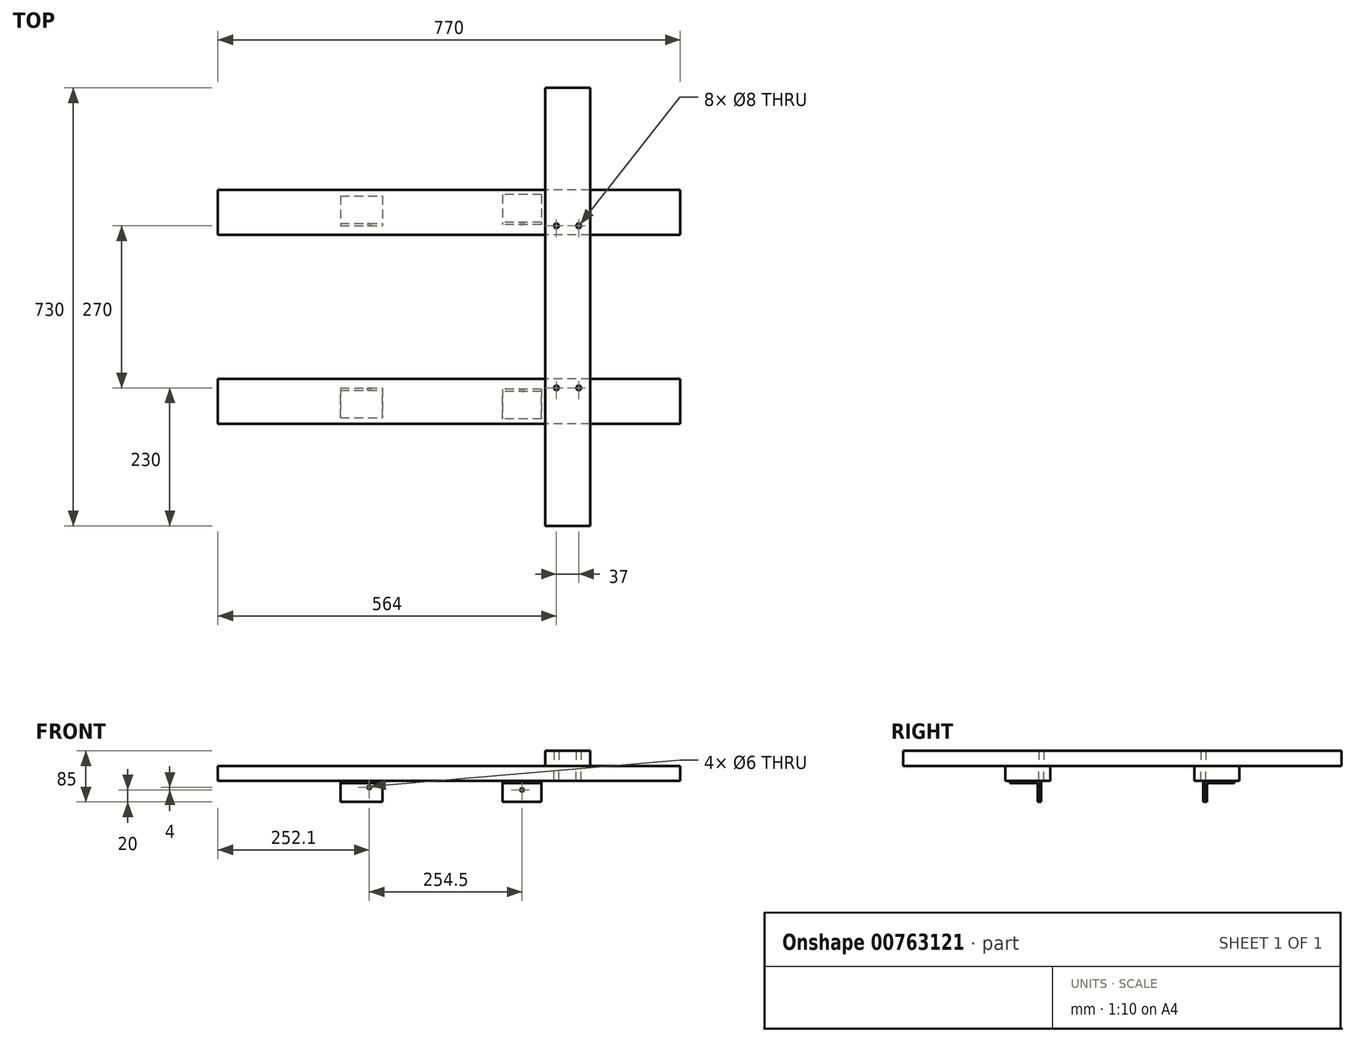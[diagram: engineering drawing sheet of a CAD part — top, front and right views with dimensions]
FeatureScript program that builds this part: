
annotation { "Feature Type Name" : "Feature", "Feature Type Description" : "" }
export const myFeature = defineFeature(function(context is Context, id is Id, definition is map)
    precondition{}
    {
        {
            var Q0;
            Q0=qCreatedBy(makeId("Top.planeOp"),FACE);
            var sketch = newSketch(context, id + "F0", { "sketchPlane" : qUnion([Q0])});
            skLineSegment(sketch, "E0.bottom", {"start": v(145.9, -365) * mm, "end": v(70.9, -365) * mm});
            skLineSegment(sketch, "E0.top", {"start": v(145.9, 365) * mm, "end": v(70.9, 365) * mm});
            skLineSegment(sketch, "E0.left", {"start": v(145.9, -365) * mm, "end": v(145.9, 365) * mm});
            skLineSegment(sketch, "E0.right", {"start": v(70.9, -365) * mm, "end": v(70.9, 365) * mm});
            skPoint(sketch, "E0.middle", {"position": v(108.4, 0) * mm});
            skLineSegment(sketch, "E1.bottom", {"start": v(295.9, 120) * mm, "end": v(-474.1, 120) * mm});
            skLineSegment(sketch, "E1.top", {"start": v(295.9, 195) * mm, "end": v(-474.1, 195) * mm});
            skLineSegment(sketch, "E1.left", {"start": v(295.9, 120) * mm, "end": v(295.9, 195) * mm});
            skLineSegment(sketch, "E1.right", {"start": v(-474.1, 120) * mm, "end": v(-474.1, 195) * mm});
            skPoint(sketch, "E1.middle", {"position": v(-89.1, 157.5) * mm});
            skLineSegment(sketch, "E2.bottom", {"start": v(295.9, -195) * mm, "end": v(-474.1, -195) * mm});
            skLineSegment(sketch, "E2.top", {"start": v(295.9, -120) * mm, "end": v(-474.1, -120) * mm});
            skLineSegment(sketch, "E2.left", {"start": v(295.9, -195) * mm, "end": v(295.9, -120) * mm});
            skLineSegment(sketch, "E2.right", {"start": v(-474.1, -195) * mm, "end": v(-474.1, -120) * mm});
            skPoint(sketch, "E2.middle", {"position": v(-89.1, -157.5) * mm});
            skPoint(sketch, "E3", {"position": v(89.9, 135) * mm});
            skPoint(sketch, "E4", {"position": v(126.9, 135) * mm});
            skPoint(sketch, "E5", {"position": v(89.9, -135) * mm});
            skPoint(sketch, "E6", {"position": v(126.9, -135) * mm});
            skSolve(sketch);
        }
        {
            var Q0;
            {var subQ5=sQuery(id+"F0.wireOp",EDGE,"E1.right");Q0=makeQuery(id+"F0.imprint","IMPRINT",FACE,{"disambiguationData":[TD([[makeQuery(id+"F0.imprint","IMPRINT",EDGE,{"derivedFrom":subQ5}),-1.0]])]});}
            var Q1;
            {var subQ0=sQuery(id+"F0.wireOp",EDGE,"E1.bottom");var subQ1=sQuery(id+"F0.wireOp",EDGE,"E0.left");var subQ2=makeQuery(id+"F0.imprint","INTERSECT",VERTEX,{"derivedFrom":[subQ1,subQ0]});Q1=makeQuery(id+"F0.imprint","IMPRINT",FACE,{"disambiguationData":[TD([[makeQuery(id+"F0.imprint","IMPRINT",EDGE,{"disambiguationData":[TD([[subQ2,-1.0]])],"derivedFrom":subQ1}),1.0]])]});}
            var Q2;
            {var subQ5=sQuery(id+"F0.wireOp",EDGE,"E1.left");Q2=makeQuery(id+"F0.imprint","IMPRINT",FACE,{"disambiguationData":[TD([[makeQuery(id+"F0.imprint","IMPRINT",EDGE,{"derivedFrom":subQ5}),1.0]])]});}
            var Q3;
            {var subQ5=sQuery(id+"F0.wireOp",EDGE,"E2.right");Q3=makeQuery(id+"F0.imprint","IMPRINT",FACE,{"disambiguationData":[TD([[makeQuery(id+"F0.imprint","IMPRINT",EDGE,{"derivedFrom":subQ5}),-1.0]])]});}
            var Q4;
            {var subQ0=sQuery(id+"F0.wireOp",EDGE,"E2.bottom");var subQ1=sQuery(id+"F0.wireOp",EDGE,"E0.left");var subQ2=makeQuery(id+"F0.imprint","INTERSECT",VERTEX,{"derivedFrom":[subQ1,subQ0]});Q4=makeQuery(id+"F0.imprint","IMPRINT",FACE,{"disambiguationData":[TD([[makeQuery(id+"F0.imprint","IMPRINT",EDGE,{"disambiguationData":[TD([[subQ2,-1.0]])],"derivedFrom":subQ1}),1.0]])]});}
            var Q5;
            {var subQ5=sQuery(id+"F0.wireOp",EDGE,"E2.left");Q5=makeQuery(id+"F0.imprint","IMPRINT",FACE,{"disambiguationData":[TD([[makeQuery(id+"F0.imprint","IMPRINT",EDGE,{"derivedFrom":subQ5}),1.0]])]});}
            extrude(context, id + "F1", {"entities" : qUnion([Q0, Q1, Q2, Q3, Q4, Q5]), "oppositeDirection" : true, "depth" : 25 * mm, "offsetDistance" : 25 * mm});
        }
        {
            var Q0;
            {var subQ0=sQuery(id+"F0.wireOp",EDGE,"E1.bottom");var subQ1=sQuery(id+"F0.wireOp",EDGE,"E0.left");var subQ2=makeQuery(id+"F0.imprint","INTERSECT",VERTEX,{"derivedFrom":[subQ1,subQ0]});Q0=makeQuery(id+"F0.imprint","IMPRINT",FACE,{"disambiguationData":[TD([[makeQuery(id+"F0.imprint","IMPRINT",EDGE,{"disambiguationData":[TD([[subQ2,-1.0]])],"derivedFrom":subQ1}),1.0]])]});}
            var Q1;
            {var subQ0=sQuery(id+"F0.wireOp",EDGE,"E0.top");Q1=makeQuery(id+"F0.imprint","IMPRINT",FACE,{"disambiguationData":[TD([[makeQuery(id+"F0.imprint","IMPRINT",EDGE,{"derivedFrom":subQ0}),1.0]])]});}
            var Q2;
            {var subQ0=sQuery(id+"F0.wireOp",EDGE,"E2.top");var subQ1=sQuery(id+"F0.wireOp",EDGE,"E0.left");var subQ2=makeQuery(id+"F0.imprint","INTERSECT",VERTEX,{"derivedFrom":[subQ1,subQ0]});Q2=makeQuery(id+"F0.imprint","IMPRINT",FACE,{"disambiguationData":[TD([[makeQuery(id+"F0.imprint","IMPRINT",EDGE,{"disambiguationData":[TD([[subQ2,-1.0]])],"derivedFrom":subQ1}),1.0]])]});}
            var Q3;
            {var subQ0=sQuery(id+"F0.wireOp",EDGE,"E2.bottom");var subQ1=sQuery(id+"F0.wireOp",EDGE,"E0.left");var subQ2=makeQuery(id+"F0.imprint","INTERSECT",VERTEX,{"derivedFrom":[subQ1,subQ0]});Q3=makeQuery(id+"F0.imprint","IMPRINT",FACE,{"disambiguationData":[TD([[makeQuery(id+"F0.imprint","IMPRINT",EDGE,{"disambiguationData":[TD([[subQ2,-1.0]])],"derivedFrom":subQ1}),1.0]])]});}
            var Q4;
            {var subQ0=sQuery(id+"F0.wireOp",EDGE,"E0.bottom");Q4=makeQuery(id+"F0.imprint","IMPRINT",FACE,{"disambiguationData":[TD([[makeQuery(id+"F0.imprint","IMPRINT",EDGE,{"derivedFrom":subQ0}),-1.0]])]});}
            extrude(context, id + "F2", {"entities" : qUnion([Q0, Q1, Q2, Q3, Q4]), "depth" : 25 * mm, "offsetDistance" : 25 * mm});
        }
        {
            var Q0;
            Q0=sQuery(id+"F0.wireOp",VERTEX,"E3");
            var Q1;
            Q1=sQuery(id+"F0.wireOp",VERTEX,"E4");
            var Q2;
            Q2=sQuery(id+"F0.wireOp",VERTEX,"E5");
            var Q3;
            Q3=sQuery(id+"F0.wireOp",VERTEX,"E6");
            var Q4;
            Q4=makeQuery(id+"F1.opExtrude","SWEPT_BODY",BODY,{"disambiguationData":[OSD([sQuery(id+"F0.wireOp",EDGE,"E1.bottom"),sQuery(id+"F0.wireOp",EDGE,"E1.top"),sQuery(id+"F0.wireOp",EDGE,"E1.left"),sQuery(id+"F0.wireOp",EDGE,"E1.right")])]});
            var Q5;
            Q5=makeQuery(id+"F1.opExtrude","SWEPT_BODY",BODY,{"disambiguationData":[OSD([sQuery(id+"F0.wireOp",EDGE,"E2.bottom"),sQuery(id+"F0.wireOp",EDGE,"E2.top"),sQuery(id+"F0.wireOp",EDGE,"E2.left"),sQuery(id+"F0.wireOp",EDGE,"E2.right")])]});
            hole(context, id + "F3", {"style" : HoleStyle.SIMPLE, "endStyle" : HoleEndStyle.THROUGH, "holeDiameter" : 8 * mm, "majorDiameter" : 5 * mm, "isTappedThrough" : true, "tappedDepth" : 12 * mm, "tapClearance" : 3, "locations" : qUnion([Q0, Q1, Q2, Q3]), "scope" : qUnion([Q4, Q5])});
        }
        {
            var Q0;
            Q0=sQuery(id+"F0.wireOp",VERTEX,"E6");
            var Q1;
            Q1=sQuery(id+"F0.wireOp",VERTEX,"E5");
            var Q2;
            Q2=sQuery(id+"F0.wireOp",VERTEX,"E4");
            var Q3;
            Q3=sQuery(id+"F0.wireOp",VERTEX,"E3");
            var Q4;
            Q4=makeQuery(id+"F2.opExtrude","SWEPT_BODY",BODY,{"disambiguationData":[OSD([sQuery(id+"F0.wireOp",EDGE,"E0.bottom"),sQuery(id+"F0.wireOp",EDGE,"E0.top"),sQuery(id+"F0.wireOp",EDGE,"E0.left"),sQuery(id+"F0.wireOp",EDGE,"E0.right")])]});
            hole(context, id + "F4", {"style" : HoleStyle.SIMPLE, "endStyle" : HoleEndStyle.THROUGH, "oppositeDirection" : true, "holeDiameter" : 8 * mm, "majorDiameter" : 5 * mm, "isTappedThrough" : true, "tappedDepth" : 12 * mm, "tapClearance" : 3, "locations" : qUnion([Q0, Q1, Q2, Q3]), "scope" : qUnion([Q4])});
        }
        {
            var Q0;
            Q0=qCreatedBy(makeId("Right.planeOp"),FACE);
            var sketch = newSketch(context, id + "F5", { "sketchPlane" : qUnion([Q0])});
            skLineSegment(sketch, "E7.bottom", {"start": v(-137, -60) * mm, "end": v(-187, -60) * mm});
            skLineSegment(sketch, "E7.top", {"start": v(-137, -25) * mm, "end": v(-187, -25) * mm});
            skLineSegment(sketch, "E7.left", {"start": v(-137, -60) * mm, "end": v(-137, -25) * mm});
            skLineSegment(sketch, "E7.right", {"start": v(-187, -60) * mm, "end": v(-187, -25) * mm});
            skPoint(sketch, "E7.middle", {"position": v(-162, -42.5) * mm});
            skLineSegment(sketch, "E8.bottom", {"start": v(-187, -60) * mm, "end": v(-141, -60) * mm});
            skLineSegment(sketch, "E8.top", {"start": v(-187, -29) * mm, "end": v(-141, -29) * mm});
            skLineSegment(sketch, "E8.left", {"start": v(-187, -60) * mm, "end": v(-187, -29) * mm});
            skLineSegment(sketch, "E8.right", {"start": v(-141, -60) * mm, "end": v(-141, -29) * mm});
            skSolve(sketch);
        }
        {
            var Q0;
            Q0=qCreatedBy(makeId("Right.planeOp"),FACE);
            var sketch = newSketch(context, id + "F6", { "sketchPlane" : qUnion([Q0])});
            skLineSegment(sketch, "E9.bottom", {"start": v(187, -25) * mm, "end": v(137, -25) * mm});
            skLineSegment(sketch, "E9.top", {"start": v(187, -60) * mm, "end": v(137, -60) * mm});
            skLineSegment(sketch, "E9.left", {"start": v(187, -25) * mm, "end": v(187, -60) * mm});
            skLineSegment(sketch, "E9.right", {"start": v(137, -25) * mm, "end": v(137, -60) * mm});
            skPoint(sketch, "E9.middle", {"position": v(162, -42.5) * mm});
            skLineSegment(sketch, "E10.bottom", {"start": v(187, -60) * mm, "end": v(141, -60) * mm});
            skLineSegment(sketch, "E10.top", {"start": v(187, -29) * mm, "end": v(141, -29) * mm});
            skLineSegment(sketch, "E10.left", {"start": v(187, -60) * mm, "end": v(187, -29) * mm});
            skLineSegment(sketch, "E10.right", {"start": v(141, -60) * mm, "end": v(141, -29) * mm});
            skSolve(sketch);
        }
        {
            var Q0;
            {var subQ1=sQuery(id+"F6.wireOp",EDGE,"E9.bottom");Q0=makeQuery(id+"F6.imprint","IMPRINT",FACE,{"disambiguationData":[TD([[makeQuery(id+"F6.imprint","IMPRINT",EDGE,{"derivedFrom":subQ1}),1.0]])]});}
            extrude(context, id + "F7", {"entities" : qUnion([Q0]), "depth" : 65 * mm, "offsetDistance" : 25 * mm});
        }
        {
            var Q0;
            Q0=makeQuery(id+"F7.opExtrude","SWEPT_FACE",FACE,{"disambiguationData":[OSD([sQuery(id+"F6.wireOp",EDGE,"E9.right")])]});
            var sketch = newSketch(context, id + "F8", { "sketchPlane" : qUnion([Q0])});
            skPoint(sketch, "E11", {"position": v(32.5, -40) * mm});
            skSolve(sketch);
        }
        {
            var Q0;
            Q0=sQuery(id+"F8.wireOp",VERTEX,"E11");
            var Q1;
            Q1=makeQuery(id+"F7.opExtrude","SWEPT_BODY",BODY,{"disambiguationData":[OSD([sQuery(id+"F6.wireOp",EDGE,"E9.bottom"),sQuery(id+"F6.wireOp",EDGE,"E9.top"),sQuery(id+"F6.wireOp",EDGE,"E9.left"),sQuery(id+"F6.wireOp",EDGE,"E9.right"),sQuery(id+"F6.wireOp",EDGE,"E10.top"),sQuery(id+"F6.wireOp",EDGE,"E10.right")])]});
            hole(context, id + "F9", {"style" : HoleStyle.SIMPLE, "endStyle" : HoleEndStyle.THROUGH, "holeDiameter" : 6 * mm, "majorDiameter" : 5 * mm, "isTappedThrough" : true, "tappedDepth" : 12 * mm, "tapClearance" : 3, "locations" : qUnion([Q0]), "scope" : qUnion([Q1])});
        }
        {
            var Q0;
            {var subQ1=sQuery(id+"F5.wireOp",EDGE,"E7.top");Q0=makeQuery(id+"F5.imprint","IMPRINT",FACE,{"disambiguationData":[TD([[makeQuery(id+"F5.imprint","IMPRINT",EDGE,{"derivedFrom":subQ1}),1.0]])]});}
            extrude(context, id + "F10", {"entities" : qUnion([Q0]), "depth" : 65 * mm, "offsetDistance" : 25 * mm});
        }
        {
            var Q0;
            Q0=makeQuery(id+"F10.opExtrude","SWEPT_FACE",FACE,{"disambiguationData":[OSD([sQuery(id+"F5.wireOp",EDGE,"E7.left")])]});
            var sketch = newSketch(context, id + "F11", { "sketchPlane" : qUnion([Q0])});
            skPoint(sketch, "E12", {"position": v(-32.5, -40) * mm});
            skSolve(sketch);
        }
        {
            var Q0;
            Q0=sQuery(id+"F11.wireOp",VERTEX,"E12");
            var Q1;
            Q1=makeQuery(id+"F10.opExtrude","SWEPT_BODY",BODY,{"disambiguationData":[OSD([sQuery(id+"F5.wireOp",EDGE,"E7.bottom"),sQuery(id+"F5.wireOp",EDGE,"E7.top"),sQuery(id+"F5.wireOp",EDGE,"E7.left"),sQuery(id+"F5.wireOp",EDGE,"E7.right"),sQuery(id+"F5.wireOp",EDGE,"E8.top"),sQuery(id+"F5.wireOp",EDGE,"E8.right")])]});
            hole(context, id + "F12", {"style" : HoleStyle.SIMPLE, "endStyle" : HoleEndStyle.THROUGH, "holeDiameter" : 6 * mm, "majorDiameter" : 5 * mm, "isTappedThrough" : true, "tappedDepth" : 12 * mm, "tapClearance" : 3, "locations" : qUnion([Q0]), "scope" : qUnion([Q1])});
        }
        {
            var Q0;
            Q0=qCreatedBy(makeId("Right.planeOp"),FACE);
            cPlane(context, id + "F13", {"entities" : qUnion([Q0]), "cplaneType" : CPlaneType.OFFSET, "offset" : 200 * mm, "oppositeDirection" : true, "width" : 150 * mm, "height" : 150 * mm});
        }
        {
            var Q0;
            Q0=qCreatedBy(id+"F13.planeOp",FACE);
            var sketch = newSketch(context, id + "F14", { "sketchPlane" : qUnion([Q0])});
            skLineSegment(sketch, "E13.bottom", {"start": v(-135, -60) * mm, "end": v(-185, -60) * mm});
            skLineSegment(sketch, "E13.top", {"start": v(-135, -25) * mm, "end": v(-185, -25) * mm});
            skLineSegment(sketch, "E13.left", {"start": v(-135, -60) * mm, "end": v(-135, -25) * mm});
            skLineSegment(sketch, "E13.right", {"start": v(-185, -60) * mm, "end": v(-185, -25) * mm});
            skPoint(sketch, "E13.middle", {"position": v(-160, -42.5) * mm});
            skLineSegment(sketch, "E14.bottom", {"start": v(-185, -60) * mm, "end": v(-139, -60) * mm});
            skLineSegment(sketch, "E14.top", {"start": v(-185, -29) * mm, "end": v(-139, -29) * mm});
            skLineSegment(sketch, "E14.left", {"start": v(-185, -60) * mm, "end": v(-185, -29) * mm});
            skLineSegment(sketch, "E14.right", {"start": v(-139, -60) * mm, "end": v(-139, -29) * mm});
            skSolve(sketch);
        }
        {
            var Q0;
            Q0=qCreatedBy(id+"F13.planeOp",FACE);
            var sketch = newSketch(context, id + "F15", { "sketchPlane" : qUnion([Q0])});
            skLineSegment(sketch, "E15.bottom", {"start": v(185, -25) * mm, "end": v(135, -25) * mm});
            skLineSegment(sketch, "E15.top", {"start": v(185, -60) * mm, "end": v(135, -60) * mm});
            skLineSegment(sketch, "E15.left", {"start": v(185, -25) * mm, "end": v(185, -60) * mm});
            skLineSegment(sketch, "E15.right", {"start": v(135, -25) * mm, "end": v(135, -60) * mm});
            skPoint(sketch, "E15.middle", {"position": v(160, -42.5) * mm});
            skLineSegment(sketch, "E16.bottom", {"start": v(185, -60) * mm, "end": v(139, -60) * mm});
            skLineSegment(sketch, "E16.top", {"start": v(185, -29) * mm, "end": v(139, -29) * mm});
            skLineSegment(sketch, "E16.left", {"start": v(185, -60) * mm, "end": v(185, -29) * mm});
            skLineSegment(sketch, "E16.right", {"start": v(139, -60) * mm, "end": v(139, -29) * mm});
            skSolve(sketch);
        }
        {
            var Q0;
            {var subQ1=sQuery(id+"F14.wireOp",EDGE,"E13.top");Q0=makeQuery(id+"F14.imprint","IMPRINT",FACE,{"disambiguationData":[TD([[makeQuery(id+"F14.imprint","IMPRINT",EDGE,{"derivedFrom":subQ1}),1.0]])]});}
            extrude(context, id + "F16", {"entities" : qUnion([Q0]), "oppositeDirection" : true, "depth" : 70 * mm, "offsetDistance" : 25 * mm});
        }
        {
            var Q0;
            {var subQ1=sQuery(id+"F15.wireOp",EDGE,"E15.bottom");Q0=makeQuery(id+"F15.imprint","IMPRINT",FACE,{"disambiguationData":[TD([[makeQuery(id+"F15.imprint","IMPRINT",EDGE,{"derivedFrom":subQ1}),1.0]])]});}
            extrude(context, id + "F17", {"entities" : qUnion([Q0]), "oppositeDirection" : true, "depth" : 70 * mm, "offsetDistance" : 25 * mm});
        }
        {
            var Q0;
            Q0=makeQuery(id+"F16.opExtrude","SWEPT_FACE",FACE,{"disambiguationData":[OSD([sQuery(id+"F14.wireOp",EDGE,"E13.left")])]});
            var sketch = newSketch(context, id + "F18", { "sketchPlane" : qUnion([Q0])});
            skPoint(sketch, "E17", {"position": v(222, -36) * mm});
            skSolve(sketch);
        }
        {
            var Q0;
            Q0=sQuery(id+"F18.wireOp",VERTEX,"E17");
            var Q1;
            Q1=makeQuery(id+"F16.opExtrude","SWEPT_BODY",BODY,{"disambiguationData":[OSD([sQuery(id+"F14.wireOp",EDGE,"E13.bottom"),sQuery(id+"F14.wireOp",EDGE,"E13.top"),sQuery(id+"F14.wireOp",EDGE,"E13.left"),sQuery(id+"F14.wireOp",EDGE,"E13.right"),sQuery(id+"F14.wireOp",EDGE,"E14.top"),sQuery(id+"F14.wireOp",EDGE,"E14.right")])]});
            hole(context, id + "F19", {"style" : HoleStyle.SIMPLE, "endStyle" : HoleEndStyle.THROUGH, "holeDiameter" : 6 * mm, "majorDiameter" : 5 * mm, "isTappedThrough" : true, "tappedDepth" : 12 * mm, "tapClearance" : 3, "locations" : qUnion([Q0]), "scope" : qUnion([Q1])});
        }
        {
            var Q0;
            Q0=makeQuery(id+"F17.opExtrude","SWEPT_FACE",FACE,{"disambiguationData":[OSD([sQuery(id+"F15.wireOp",EDGE,"E15.right")])]});
            var sketch = newSketch(context, id + "F20", { "sketchPlane" : qUnion([Q0])});
            skPoint(sketch, "E18", {"position": v(-222, -36) * mm});
            skSolve(sketch);
        }
        {
            var Q0;
            Q0=sQuery(id+"F20.wireOp",VERTEX,"E18");
            var Q1;
            Q1=makeQuery(id+"F17.opExtrude","SWEPT_BODY",BODY,{"disambiguationData":[OSD([sQuery(id+"F15.wireOp",EDGE,"E15.bottom"),sQuery(id+"F15.wireOp",EDGE,"E15.top"),sQuery(id+"F15.wireOp",EDGE,"E15.left"),sQuery(id+"F15.wireOp",EDGE,"E15.right"),sQuery(id+"F15.wireOp",EDGE,"E16.top"),sQuery(id+"F15.wireOp",EDGE,"E16.right")])]});
            hole(context, id + "F21", {"style" : HoleStyle.SIMPLE, "endStyle" : HoleEndStyle.THROUGH, "holeDiameter" : 6 * mm, "majorDiameter" : 5 * mm, "isTappedThrough" : true, "tappedDepth" : 12 * mm, "tapClearance" : 3, "locations" : qUnion([Q0]), "scope" : qUnion([Q1])});
        }
    });
